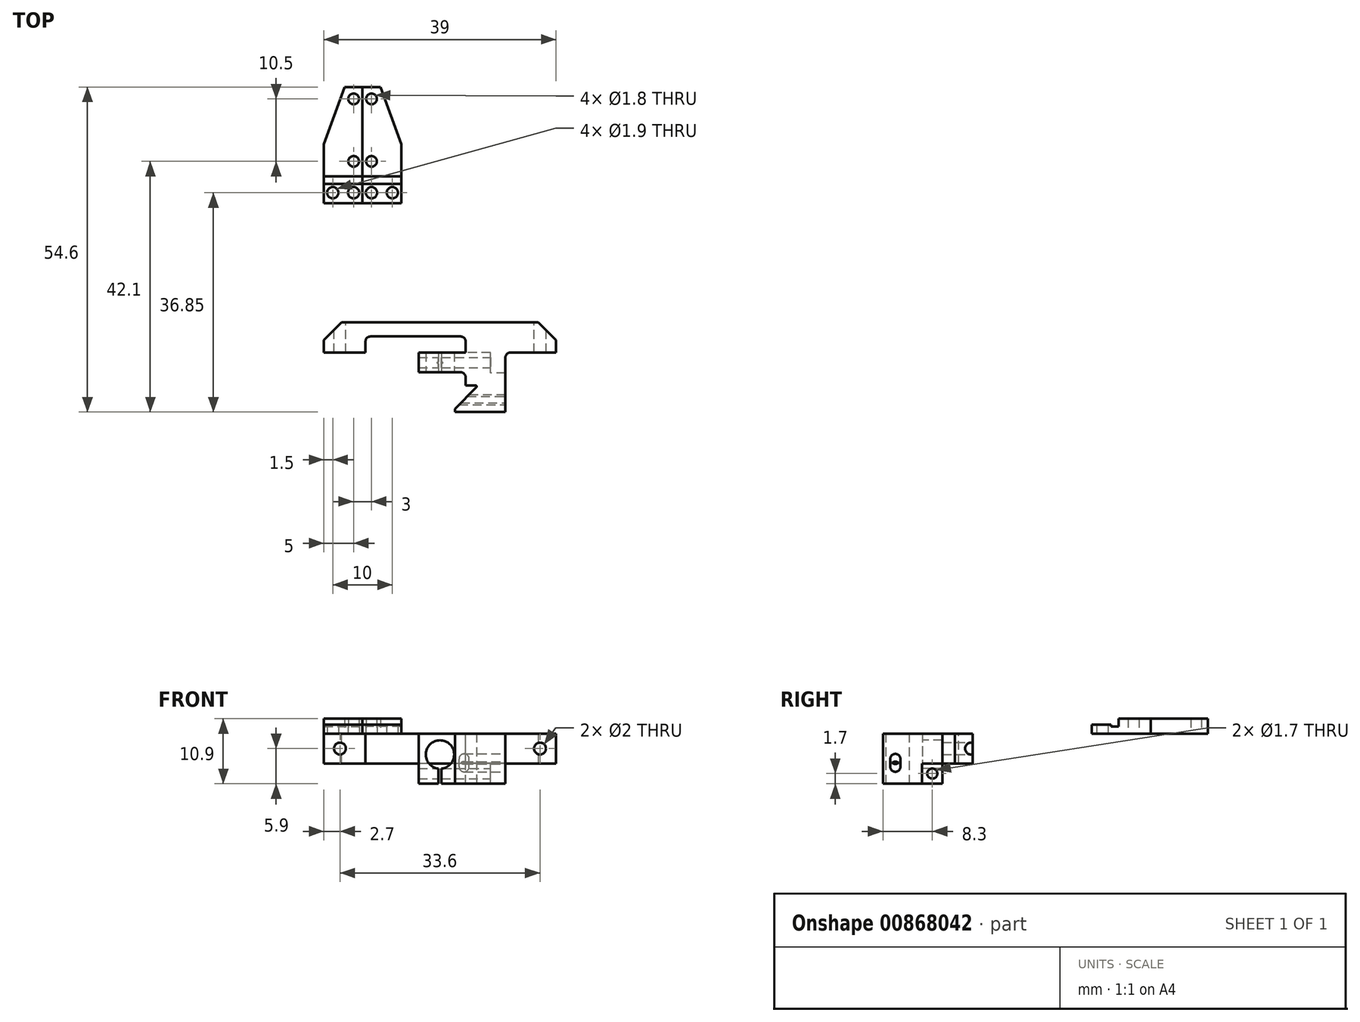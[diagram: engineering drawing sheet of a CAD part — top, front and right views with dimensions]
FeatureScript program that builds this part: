
annotation { "Feature Type Name" : "Feature", "Feature Type Description" : "" }
export const myFeature = defineFeature(function(context is Context, id is Id, definition is map)
    precondition{}
    {
        {
            var Q0;
            Q0=qCreatedBy(makeId("Top.planeOp"),FACE);
            var sketch = newSketch(context, id + "F0", { "sketchPlane" : qUnion([Q0])});
            skLineSegment(sketch, "E0", {"start": v(0, 0) * mm, "end": v(6.5, 0) * mm});
            skLineSegment(sketch, "E1", {"start": v(6.5, 0) * mm, "end": v(6.5, 19.5) * mm});
            skLineSegment(sketch, "E2", {"start": v(6.5, 19.5) * mm, "end": v(3.5, 19.5) * mm});
            skLineSegment(sketch, "E3", {"start": v(0, 9.88) * mm, "end": v(3.5, 19.5) * mm});
            skLineSegment(sketch, "E4", {"start": v(0, 9.88) * mm, "end": v(0, 0) * mm});
            skLineSegment(sketch, "E5", {"start": v(5, 17.5) * mm, "end": v(5, 1.75) * mm, "construction": true});
            skLineSegment(sketch, "E6", {"start": v(5, 1.75) * mm, "end": v(1.5, 1.75) * mm, "construction": true});
            skPoint(sketch, "E7", {"position": v(5, 7) * mm});
            skLineSegment(sketch, "E8", {"start": v(0, 3.2) * mm, "end": v(6.5, 3.2) * mm});
            skCircle(sketch, "E9", {"center": v(5, 17.5) * mm, "radius": 0.9 * mm});
            skCircle(sketch, "E10", {"center": v(5, 7) * mm, "radius": 0.9 * mm});
            skCircle(sketch, "E11", {"center": v(1.5, 1.75) * mm, "radius": 0.95 * mm});
            skCircle(sketch, "E12", {"center": v(5, 1.75) * mm, "radius": 0.95 * mm});
            skLineSegment(sketch, "E13", {"start": v(0, 4.5) * mm, "end": v(6.5, 4.5) * mm});
            skLineSegment(sketch, "E14", {"start": v(0, -25.1) * mm, "end": v(0, -20) * mm});
            skLineSegment(sketch, "E15", {"start": v(0, -20) * mm, "end": v(39, -20) * mm});
            skLineSegment(sketch, "E16", {"start": v(39, -20) * mm, "end": v(39, -25.1) * mm});
            skLineSegment(sketch, "E17", {"start": v(39, -25.1) * mm, "end": v(30.5, -25.1) * mm});
            skLineSegment(sketch, "E18", {"start": v(30.5, -25.1) * mm, "end": v(30.5, -35.1) * mm});
            skLineSegment(sketch, "E19", {"start": v(30.5, -35.1) * mm, "end": v(22, -35.1) * mm});
            skLineSegment(sketch, "E20", {"start": v(22, -35.1) * mm, "end": v(22, -34.55) * mm});
            skLineSegment(sketch, "E21", {"start": v(22, -34.55) * mm, "end": v(25.95, -30.6) * mm});
            skLineSegment(sketch, "E22", {"start": v(25.95, -30.6) * mm, "end": v(23.8, -30.6) * mm});
            skLineSegment(sketch, "E23", {"start": v(23.8, -30.6) * mm, "end": v(23.8, -28.4) * mm});
            skLineSegment(sketch, "E24", {"start": v(23.8, -28.4) * mm, "end": v(15.9, -28.4) * mm});
            skLineSegment(sketch, "E25", {"start": v(15.9, -28.4) * mm, "end": v(15.9, -25.1) * mm});
            skLineSegment(sketch, "E26", {"start": v(15.9, -25.1) * mm, "end": v(23.8, -25.1) * mm});
            skLineSegment(sketch, "E27", {"start": v(23.8, -25.1) * mm, "end": v(23.8, -22.4) * mm});
            skLineSegment(sketch, "E28", {"start": v(23.8, -22.4) * mm, "end": v(7, -22.4) * mm});
            skLineSegment(sketch, "E29", {"start": v(7, -22.4) * mm, "end": v(7, -25.1) * mm});
            skLineSegment(sketch, "E30", {"start": v(7, -25.1) * mm, "end": v(0, -25.1) * mm});
            skCircle(sketch, "E31", {"center": v(24.03, -31.4) * mm, "radius": 0.8 * mm, "construction": true});
            skLineSegment(sketch, "E32", {"start": v(19.5, -8.3) * mm, "end": v(19.5, -49.94) * mm, "construction": true});
            skLineSegment(sketch, "E33", {"start": v(30.5, -28.5) * mm, "end": v(28, -28.5) * mm});
            skLineSegment(sketch, "E34", {"start": v(28, -28.5) * mm, "end": v(28, -25.1) * mm});
            skLineSegment(sketch, "E35", {"start": v(28, -25.1) * mm, "end": v(23.8, -25.1) * mm});
            skLineSegment(sketch, "E36", {"start": v(-29.69, -4.65) * mm, "end": v(-46.45, -4.65) * mm});
            skLineSegment(sketch, "E37", {"start": v(-46.45, -4.65) * mm, "end": v(-46.45, -20.24) * mm});
            skLineSegment(sketch, "E38", {"start": v(-46.45, -20.24) * mm, "end": v(-35.15, -20.24) * mm});
            skLineSegment(sketch, "E39", {"start": v(-35.15, -20.24) * mm, "end": v(-35.15, -18.97) * mm});
            skLineSegment(sketch, "E40", {"start": v(-35.15, -18.97) * mm, "end": v(-40.4, -14.98) * mm});
            skLineSegment(sketch, "E41", {"start": v(-40.4, -14.98) * mm, "end": v(-29.69, -14.98) * mm});
            skLineSegment(sketch, "E42", {"start": v(-29.69, -14.98) * mm, "end": v(-29.69, -13.22) * mm});
            skLineSegment(sketch, "E43", {"start": v(-29.69, -13.22) * mm, "end": v(-38.17, -13.22) * mm});
            skLineSegment(sketch, "E44", {"start": v(-38.17, -13.22) * mm, "end": v(-38.17, -6.84) * mm});
            skLineSegment(sketch, "E45", {"start": v(-38.17, -6.84) * mm, "end": v(-29.69, -6.84) * mm});
            skLineSegment(sketch, "E46", {"start": v(-29.69, -6.84) * mm, "end": v(-29.69, -4.65) * mm});
            skLineSegment(sketch, "E47", {"start": v(-46.45, -16.67) * mm, "end": v(-38.18, -16.67) * mm});
            skLineSegment(sketch, "E48", {"start": v(-36.86, -19.38) * mm, "end": v(-46.45, -19.38) * mm});
            skLineSegment(sketch, "E49", {"start": v(-40.4, -14.98) * mm, "end": v(-46.45, -14.98) * mm});
            skLineSegment(sketch, "E50", {"start": v(-36.86, -17.67) * mm, "end": v(-36.86, -19.38) * mm});
            skSolve(sketch);
        }
        {
            var Q0;
            {var subQ3=sQuery(id+"F0.wireOp",EDGE,"E2");Q0=makeQuery(id+"F0.imprint","IMPRINT",FACE,{"disambiguationData":[TD([[makeQuery(id+"F0.imprint","IMPRINT",EDGE,{"derivedFrom":subQ3}),1.0]])]});}
            extrude(context, id + "F1", {"entities" : qUnion([Q0]), "depth" : 2.5 * mm, "offsetDistance" : 25 * mm});
        }
        {
            var Q0;
            {var subQ0=sQuery(id+"F0.wireOp",EDGE,"E8");Q0=makeQuery(id+"F0.imprint","IMPRINT",FACE,{"disambiguationData":[TD([[makeQuery(id+"F0.imprint","IMPRINT",EDGE,{"derivedFrom":subQ0}),1.0]])]});}
            extrude(context, id + "F2", {"entities" : qUnion([Q0]), "operationType" : NewBodyOperationType.ADD, "depth" : 1.2 * mm, "offsetDistance" : 25 * mm});
        }
        {
            var Q0;
            {var subQ2=sQuery(id+"F0.wireOp",EDGE,"E0");Q0=makeQuery(id+"F0.imprint","IMPRINT",FACE,{"disambiguationData":[TD([[makeQuery(id+"F0.imprint","IMPRINT",EDGE,{"derivedFrom":subQ2}),1.0]])]});}
            extrude(context, id + "F3", {"entities" : qUnion([Q0]), "operationType" : NewBodyOperationType.ADD, "depth" : 1.5 * mm, "offsetDistance" : 25 * mm});
        }
        {
            var Q0;
            Q0=makeQuery(id+"F1.opExtrude","SWEPT_BODY",BODY,{"disambiguationData":[OSD([sQuery(id+"F0.wireOp",EDGE,"E1"),sQuery(id+"F0.wireOp",EDGE,"E2"),sQuery(id+"F0.wireOp",EDGE,"E3"),sQuery(id+"F0.wireOp",EDGE,"E4"),sQuery(id+"F0.wireOp",EDGE,"E9"),sQuery(id+"F0.wireOp",EDGE,"E10"),sQuery(id+"F0.wireOp",EDGE,"E13")])]});
            var Q1;
            {var subQ0=sQuery(id+"F0.wireOp",EDGE,"E1");Q1=makeQuery(id+"F3.boolean.opBoolean","MERGE",FACE,{"derivedFrom":[makeQuery(id+"F2.boolean.opBoolean","MERGE",FACE,{"derivedFrom":[makeQuery(id+"F1.opExtrude","SWEPT_FACE",FACE,{"disambiguationData":[OSD([subQ0])]}),makeQuery(id+"F2.opExtrude","SWEPT_FACE",FACE,{"disambiguationData":[OSD([subQ0])]})]}),makeQuery(id+"F3.opExtrude","SWEPT_FACE",FACE,{"disambiguationData":[OSD([subQ0])]})]});}
            mirror(context, id + "F4", {"entities" : qUnion([Q0]), "mirrorPlane" : qUnion([Q1])});
        }
        {
            var Q0;
            Q0=makeQuery(id+"F0.imprint","IMPRINT",FACE,{"disambiguationData":[TD([[makeQuery(id+"F0.imprint","IMPRINT",EDGE,{"derivedFrom":sQuery(id+"F0.wireOp",EDGE,"E14")}),-1.0]])]});
            var Q1;
            {var subQ3=sQuery(id+"F0.wireOp",EDGE,"E16");Q1=makeQuery(id+"F0.imprint","IMPRINT",FACE,{"disambiguationData":[TD([[makeQuery(id+"F0.imprint","IMPRINT",EDGE,{"derivedFrom":subQ3}),-1.0]])]});}
            extrude(context, id + "F5", {"entities" : qUnion([Q0, Q1]), "oppositeDirection" : true, "depth" : 5 * mm, "offsetDistance" : 25 * mm});
        }
        {
            var Q0;
            {var subQ0=sQuery(id+"F0.wireOp",EDGE,"E19");Q0=makeQuery(id+"F0.imprint","IMPRINT",FACE,{"disambiguationData":[TD([[makeQuery(id+"F0.imprint","IMPRINT",EDGE,{"derivedFrom":subQ0}),-1.0]])]});}
            var Q1;
            {var subQ0=sQuery(id+"F0.wireOp",EDGE,"E25");Q1=makeQuery(id+"F0.imprint","IMPRINT",FACE,{"disambiguationData":[TD([[makeQuery(id+"F0.imprint","IMPRINT",EDGE,{"derivedFrom":subQ0}),-1.0]])]});}
            extrude(context, id + "F6", {"entities" : qUnion([Q0, Q1]), "operationType" : NewBodyOperationType.ADD, "oppositeDirection" : true, "depth" : 8.4 * mm, "offsetDistance" : 25 * mm});
        }
        {
            var Q0;
            Q0=makeQuery(id+"F5.opExtrude","SWEPT_FACE",FACE,{"disambiguationData":[OSD([sQuery(id+"F0.wireOp",EDGE,"E15")])]});
            var sketch = newSketch(context, id + "F7", { "sketchPlane" : qUnion([Q0])});
            skLineSegment(sketch, "E51", {"start": v(-36.3, -2.5) * mm, "end": v(-2.7, -2.5) * mm, "construction": true});
            skSolve(sketch);
        }
        {
            var Q0;
            Q0=sQuery(id+"F7.wireOp",VERTEX,"E51.end");
            var Q1;
            Q1=sQuery(id+"F7.wireOp",VERTEX,"E51.start");
            var Q2;
            Q2=makeQuery(id+"F5.opExtrude","SWEPT_BODY",BODY,{"disambiguationData":[OSD([sQuery(id+"F0.wireOp",EDGE,"E14"),sQuery(id+"F0.wireOp",EDGE,"E15"),sQuery(id+"F0.wireOp",EDGE,"E16"),sQuery(id+"F0.wireOp",EDGE,"E17"),sQuery(id+"F0.wireOp",EDGE,"E18"),sQuery(id+"F0.wireOp",EDGE,"E27"),sQuery(id+"F0.wireOp",EDGE,"E28"),sQuery(id+"F0.wireOp",EDGE,"E29"),sQuery(id+"F0.wireOp",EDGE,"E30"),sQuery(id+"F0.wireOp",EDGE,"E33"),sQuery(id+"F0.wireOp",EDGE,"E34"),sQuery(id+"F0.wireOp",EDGE,"E35")])]});
            hole(context, id + "F8", {"style" : HoleStyle.SIMPLE, "endStyle" : HoleEndStyle.BLIND, "standardTappedOrClearance" : lookupTablePath({ "standard" : "ISO", "size" : "2", "type" : "Drilled" }), "standardBlindInLast" : lookupTablePath({ "standard" : "ISO", "size" : "2", "type" : "Drilled" }), "holeDiameter" : 2 * mm, "majorDiameter" : 5 * mm, "holeDepth" : 14.4 * mm, "tappedDepth" : 12 * mm, "tapClearance" : 3, "startFromSketch" : true, "locations" : qUnion([Q0, Q1]), "scope" : qUnion([Q2])});
        }
        {
            var Q0;
            Q0=makeQuery(id+"F6.opExtrude","SWEPT_FACE",FACE,{"disambiguationData":[OSD([sQuery(id+"F0.wireOp",EDGE,"E24")])]});
            var sketch = newSketch(context, id + "F9", { "sketchPlane" : qUnion([Q0])});
            skCircle(sketch, "E52", {"center": v(19.5, -3.5) * mm, "radius": 2.4 * mm});
            skLineSegment(sketch, "E53.bottom", {"start": v(19.75, -8.4) * mm, "end": v(19.25, -8.4) * mm});
            skLineSegment(sketch, "E53.top", {"start": v(19.75, -5.88) * mm, "end": v(19.25, -5.88) * mm});
            skLineSegment(sketch, "E53.left", {"start": v(19.75, -8.4) * mm, "end": v(19.75, -5.88) * mm});
            skLineSegment(sketch, "E53.right", {"start": v(19.25, -8.4) * mm, "end": v(19.25, -5.88) * mm});
            skPoint(sketch, "E53.middle", {"position": v(19.5, -7.14) * mm});
            skSolve(sketch);
        }
        {
            var Q0;
            {var subQ0=sQuery(id+"F9.wireOp",EDGE,"E53.top");Q0=makeQuery(id+"F9.imprint","IMPRINT",FACE,{"disambiguationData":[TD([[makeQuery(id+"F9.imprint","IMPRINT",EDGE,{"derivedFrom":subQ0}),-1.0]])]});}
            var Q1;
            Q1=makeQuery(id+"F9.imprint","IMPRINT",FACE,{"disambiguationData":[TD([[makeQuery(id+"F9.imprint","IMPRINT",EDGE,{"derivedFrom":sQuery(id+"F9.wireOp",EDGE,"E53.bottom")}),-1.0]])]});
            var Q2;
            {var subQ0=sQuery(id+"F9.wireOp",EDGE,"E53.top");Q2=makeQuery(id+"F9.imprint","IMPRINT",FACE,{"disambiguationData":[TD([[makeQuery(id+"F9.imprint","IMPRINT",EDGE,{"derivedFrom":subQ0}),1.0]])]});}
            extrude(context, id + "F10", {"entities" : qUnion([Q0, Q1, Q2]), "operationType" : NewBodyOperationType.REMOVE, "oppositeDirection" : true, "depth" : 3.8 * mm, "offsetDistance" : 25 * mm});
        }
        {
            var Q0;
            {var subQ0=sQuery(id+"F0.wireOp",EDGE,"E18");Q0=makeQuery(id+"F6.boolean.opBoolean","MERGE",FACE,{"derivedFrom":[makeQuery(id+"F5.opExtrude","SWEPT_FACE",FACE,{"disambiguationData":[OSD([subQ0])]}),makeQuery(id+"F6.opExtrude","SWEPT_FACE",FACE,{"disambiguationData":[OSD([subQ0])]})]});}
            var sketch = newSketch(context, id + "F11", { "sketchPlane" : qUnion([Q0])});
            skCircle(sketch, "E54", {"center": v(-26.8, -6.7) * mm, "radius": 0.85 * mm});
            skPoint(sketch, "E54.centerSnap0", {"position": v(-25.1, -6.7) * mm});
            skPoint(sketch, "E54.centerSnap1", {"position": v(-26.8, -8.4) * mm});
            skLineSegment(sketch, "E55.bottom", {"start": v(-32.15, -5.55) * mm, "end": v(-33.85, -5.55) * mm});
            skLineSegment(sketch, "E55.top", {"start": v(-32.15, -4.25) * mm, "end": v(-33.85, -4.25) * mm});
            skLineSegment(sketch, "E55.left", {"start": v(-32.15, -5.55) * mm, "end": v(-32.15, -4.25) * mm});
            skLineSegment(sketch, "E55.right", {"start": v(-33.85, -5.55) * mm, "end": v(-33.85, -4.25) * mm});
            skPoint(sketch, "E55.middle", {"position": v(-33, -4.9) * mm});
            skCircle(sketch, "E56", {"center": v(-33, -4.25) * mm, "radius": 0.85 * mm});
            skCircle(sketch, "E57", {"center": v(-33, -5.55) * mm, "radius": 0.85 * mm});
            skSolve(sketch);
        }
        {
            var Q0;
            Q0=makeQuery(id+"F11.imprint","IMPRINT",FACE,{"disambiguationData":[TD([[makeQuery(id+"F11.imprint","IMPRINT",EDGE,{"derivedFrom":sQuery(id+"F11.wireOp",EDGE,"E54")}),1.0]])]});
            var Q1;
            {var subQ0=sQuery(id+"F11.wireOp",EDGE,"E55.top");Q1=makeQuery(id+"F11.imprint","IMPRINT",FACE,{"disambiguationData":[TD([[makeQuery(id+"F11.imprint","IMPRINT",EDGE,{"derivedFrom":subQ0}),-1.0]])]});}
            var Q2;
            {var subQ0=sQuery(id+"F11.wireOp",EDGE,"E55.top");Q2=makeQuery(id+"F11.imprint","IMPRINT",FACE,{"disambiguationData":[TD([[makeQuery(id+"F11.imprint","IMPRINT",EDGE,{"derivedFrom":subQ0}),1.0]])]});}
            var Q3;
            {var subQ0=sQuery(id+"F11.wireOp",EDGE,"E55.right");Q3=makeQuery(id+"F11.imprint","IMPRINT",FACE,{"disambiguationData":[TD([[makeQuery(id+"F11.imprint","IMPRINT",EDGE,{"derivedFrom":subQ0}),-1.0]])]});}
            var Q4;
            {var subQ0=sQuery(id+"F11.wireOp",EDGE,"E55.bottom");Q4=makeQuery(id+"F11.imprint","IMPRINT",FACE,{"disambiguationData":[TD([[makeQuery(id+"F11.imprint","IMPRINT",EDGE,{"derivedFrom":subQ0}),-1.0]])]});}
            var Q5;
            {var subQ0=sQuery(id+"F11.wireOp",EDGE,"E57");var subQ1=sQuery(id+"F11.wireOp",EDGE,"E56");var subQ2=makeQuery(id+"F11.imprint","INTERSECT",VERTEX,{"disambiguationData":[OD(0.0)],"derivedFrom":[subQ1,subQ0]});Q5=makeQuery(id+"F11.imprint","IMPRINT",FACE,{"disambiguationData":[TD([[makeQuery(id+"F11.imprint","IMPRINT",EDGE,{"disambiguationData":[TD([[subQ2,-1.0]])],"derivedFrom":subQ1}),1.0]])]});}
            var Q6;
            {var subQ0=sQuery(id+"F11.wireOp",EDGE,"E55.left");Q6=makeQuery(id+"F11.imprint","IMPRINT",FACE,{"disambiguationData":[TD([[makeQuery(id+"F11.imprint","IMPRINT",EDGE,{"derivedFrom":subQ0}),1.0]])]});}
            var Q7;
            {var subQ0=sQuery(id+"F11.wireOp",EDGE,"E55.bottom");Q7=makeQuery(id+"F11.imprint","IMPRINT",FACE,{"disambiguationData":[TD([[makeQuery(id+"F11.imprint","IMPRINT",EDGE,{"derivedFrom":subQ0}),1.0]])]});}
            extrude(context, id + "F12", {"entities" : qUnion([Q0, Q1, Q2, Q3, Q4, Q5, Q6, Q7]), "operationType" : NewBodyOperationType.REMOVE, "endBound" : BoundingType.THROUGH_ALL, "oppositeDirection" : true, "depth" : 25 * mm, "offsetDistance" : 25 * mm});
        }
        {
            var Q0;
            Q0=makeQuery(id+"F5.opExtrude","CAP_EDGE",EDGE,{"disambiguationData":[OSD([sQuery(id+"F0.wireOp",EDGE,"E33")])],"isStart":false});
            var Q1;
            Q1=makeQuery(id+"F5.opExtrude","SWEPT_EDGE",EDGE,{"disambiguationData":[OSD([sQuery(id+"F0.wireOp",EDGE,"E28"),sQuery(id+"F0.wireOp",EDGE,"E29")])]});
            var Q2;
            Q2=makeQuery(id+"F5.opExtrude","SWEPT_EDGE",EDGE,{"disambiguationData":[OSD([sQuery(id+"F0.wireOp",EDGE,"E27"),sQuery(id+"F0.wireOp",EDGE,"E28")])]});
            var Q3;
            Q3=makeQuery(id+"F5.opExtrude","SWEPT_EDGE",EDGE,{"disambiguationData":[OSD([sQuery(id+"F0.wireOp",EDGE,"E26"),sQuery(id+"F0.wireOp",EDGE,"E27"),sQuery(id+"F0.wireOp",EDGE,"E35")])]});
            var Q4;
            Q4=makeQuery(id+"F5.opExtrude","SWEPT_EDGE",EDGE,{"disambiguationData":[OSD([sQuery(id+"F0.wireOp",EDGE,"E17"),sQuery(id+"F0.wireOp",EDGE,"E18")])]});
            var Q5;
            Q5=makeQuery(id+"F6.opExtrude","SWEPT_EDGE",EDGE,{"disambiguationData":[OSD([sQuery(id+"F0.wireOp",EDGE,"E23"),sQuery(id+"F0.wireOp",EDGE,"E24")])]});
            fillet(context, id + "F13", {"entities" : qUnion([Q0, Q1, Q2, Q3, Q4, Q5]), "radius" : .8 * mm, "tangentPropagation" : true, "allowEdgeOverflow" : false});
        }
        {
            var Q0;
            Q0=makeQuery(id+"F5.opExtrude","SWEPT_EDGE",EDGE,{"disambiguationData":[OSD([sQuery(id+"F0.wireOp",EDGE,"E14"),sQuery(id+"F0.wireOp",EDGE,"E15")])]});
            var Q1;
            Q1=makeQuery(id+"F5.opExtrude","SWEPT_EDGE",EDGE,{"disambiguationData":[OSD([sQuery(id+"F0.wireOp",EDGE,"E15"),sQuery(id+"F0.wireOp",EDGE,"E16")])]});
            chamfer(context, id + "F14", {"entities" : qUnion([Q0, Q1]), "width" : 3 * mm, "tangentPropagation" : true});
        }
        {
            var Q0;
            Q0=makeQuery(id+"F6.opExtrude","SWEPT_EDGE",EDGE,{"disambiguationData":[OSD([sQuery(id+"F0.wireOp",EDGE,"E21"),sQuery(id+"F0.wireOp",EDGE,"E22")])]});
            fillet(context, id + "F15", {"entities" : qUnion([Q0]), "radius" : .2 * mm, "tangentPropagation" : true, "allowEdgeOverflow" : false});
        }
    });
